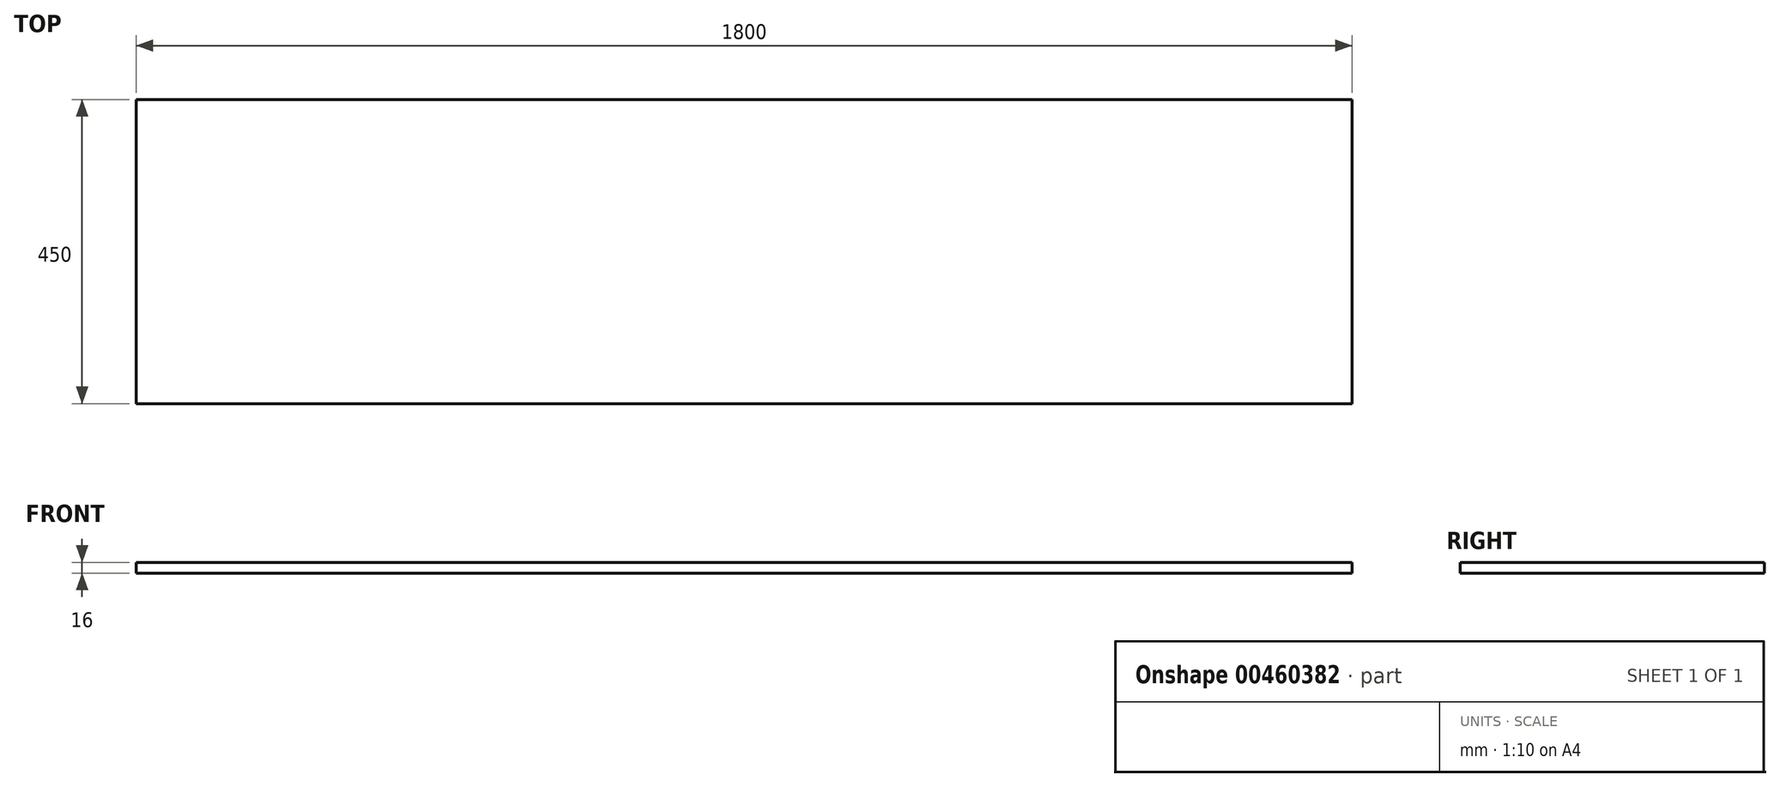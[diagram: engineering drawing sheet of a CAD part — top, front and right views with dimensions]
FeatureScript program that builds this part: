
annotation { "Feature Type Name" : "Feature", "Feature Type Description" : "" }
export const myFeature = defineFeature(function(context is Context, id is Id, definition is map)
    precondition{}
    {
        {
            var Q0;
            Q0=qCreatedBy(makeId("Top.planeOp"),FACE);
            var sketch = newSketch(context, id + "F0", { "sketchPlane" : qUnion([Q0])});
            skLineSegment(sketch, "E0.bottom", {"start": v(-894.45, 96.7) * mm, "end": v(905.55, 96.7) * mm});
            skLineSegment(sketch, "E0.top", {"start": v(-894.45, -353.3) * mm, "end": v(905.55, -353.3) * mm});
            skLineSegment(sketch, "E0.left", {"start": v(-894.45, 96.7) * mm, "end": v(-894.45, -353.3) * mm});
            skLineSegment(sketch, "E0.right", {"start": v(905.55, 96.7) * mm, "end": v(905.55, -353.3) * mm});
            skSolve(sketch);
        }
        {
            var Q0;
            Q0=makeQuery(id+"F0.imprint","IMPRINT",FACE,{"disambiguationData":[TD([[makeQuery(id+"F0.imprint","IMPRINT",EDGE,{"derivedFrom":sQuery(id+"F0.wireOp",EDGE,"E0.bottom")}),-1.0]])]});
            extrude(context, id + "F1", {"entities" : qUnion([Q0]), "depth" : 16 * mm});
        }
    });
